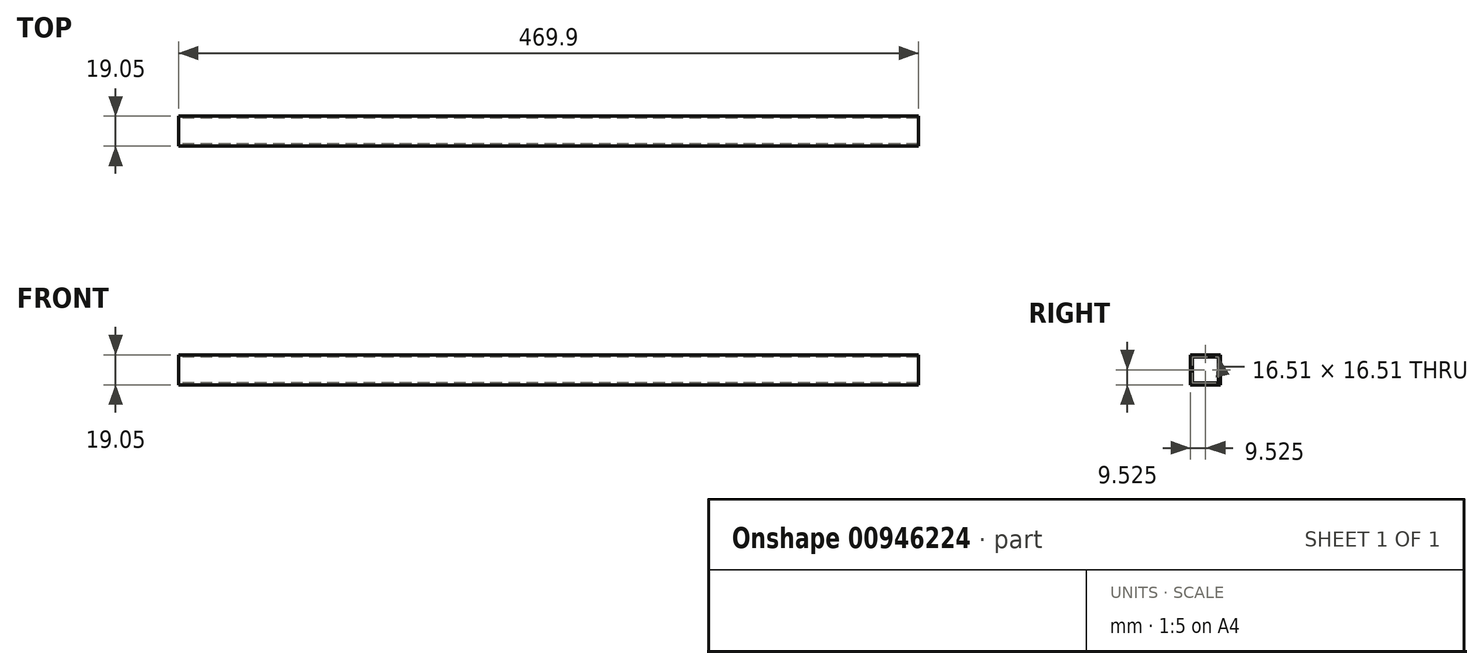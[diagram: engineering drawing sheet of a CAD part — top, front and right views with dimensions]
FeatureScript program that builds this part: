
annotation { "Feature Type Name" : "Feature", "Feature Type Description" : "" }
export const myFeature = defineFeature(function(context is Context, id is Id, definition is map)
    precondition{}
    {
        {
            var Q0;
            Q0=qCreatedBy(makeId("Right.planeOp"),FACE);
            var sketch = newSketch(context, id + "F0", { "sketchPlane" : qUnion([Q0])});
            skLineSegment(sketch, "E0.bottom", {"start": v(0, 0) * mm, "end": v(19.05, 0) * mm});
            skLineSegment(sketch, "E0.top", {"start": v(0, 19.05) * mm, "end": v(19.05, 19.05) * mm});
            skLineSegment(sketch, "E0.left", {"start": v(0, 0) * mm, "end": v(0, 19.05) * mm});
            skLineSegment(sketch, "E0.right", {"start": v(19.05, 0) * mm, "end": v(19.05, 19.05) * mm});
            skSolve(sketch);
        }
        {
            var Q0;
            Q0 = qSketchRegion(id + "F0", true);
            extrude(context, id + "F1", {"entities" : qUnion([Q0]), "depth" : 469.9 * mm, "offsetDistance" : 25.4 * mm});
        }
        {
            var Q0;
            Q0=makeQuery(id+"F1.opExtrude","CAP_FACE",FACE,{"disambiguationData":[OSD([sQuery(id+"F0.wireOp",EDGE,"E0.bottom"),sQuery(id+"F0.wireOp",EDGE,"E0.top"),sQuery(id+"F0.wireOp",EDGE,"E0.left"),sQuery(id+"F0.wireOp",EDGE,"E0.right")])],"isStart":true});
            var sketch = newSketch(context, id + "F2", { "sketchPlane" : qUnion([Q0])});
            skLineSegment(sketch, "E1.bottom", {"start": v(-1.27, 1.27) * mm, "end": v(-17.78, 1.27) * mm});
            skLineSegment(sketch, "E1.top", {"start": v(-1.27, 17.78) * mm, "end": v(-17.78, 17.78) * mm});
            skLineSegment(sketch, "E1.left", {"start": v(-1.27, 1.27) * mm, "end": v(-1.27, 17.78) * mm});
            skLineSegment(sketch, "E1.right", {"start": v(-17.78, 1.27) * mm, "end": v(-17.78, 17.78) * mm});
            skSolve(sketch);
        }
        {
            var Q0;
            Q0 = qSketchRegion(id + "F2", true);
            extrude(context, id + "F3", {"entities" : qUnion([Q0]), "operationType" : NewBodyOperationType.REMOVE, "oppositeDirection" : true, "depth" : 469.9 * mm, "offsetDistance" : 25.4 * mm});
        }
    });
